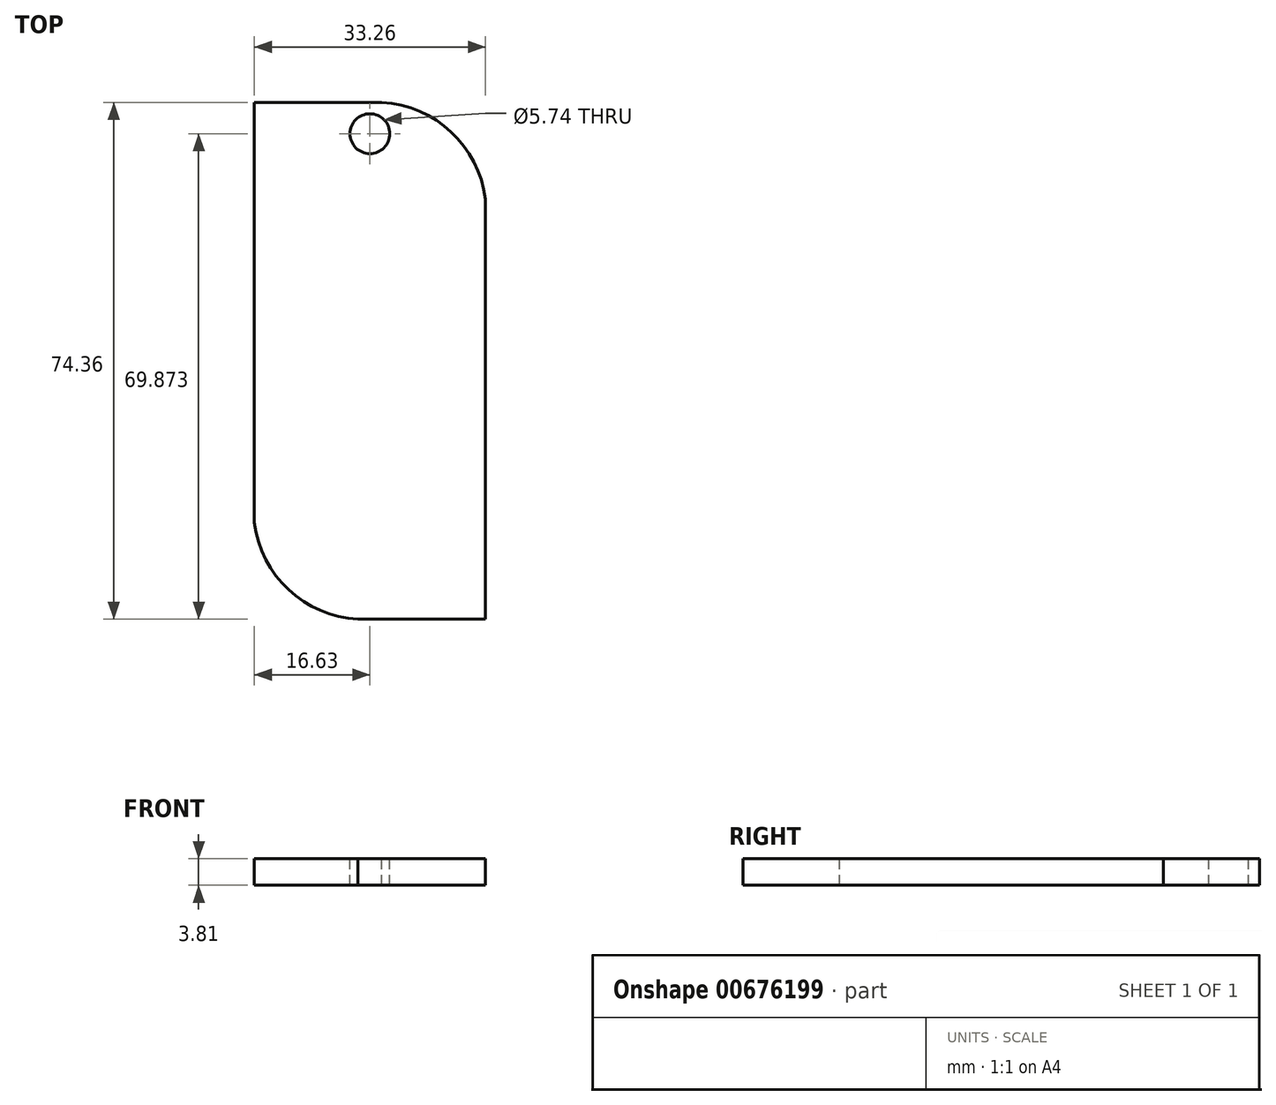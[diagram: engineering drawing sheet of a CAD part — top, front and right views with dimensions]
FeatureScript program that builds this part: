
annotation { "Feature Type Name" : "Feature", "Feature Type Description" : "" }
export const myFeature = defineFeature(function(context is Context, id is Id, definition is map)
    precondition{}
    {
        {
            var Q0;
            Q0=qCreatedBy(makeId("Top.planeOp"),FACE);
            var sketch = newSketch(context, id + "F0", { "sketchPlane" : qUnion([Q0])});
            skLineSegment(sketch, "E0.bottom", {"start": v(-16.63, 37.18) * mm, "end": v(16.63, 37.18) * mm});
            skLineSegment(sketch, "E0.top", {"start": v(-16.63, -37.18) * mm, "end": v(16.63, -37.18) * mm});
            skLineSegment(sketch, "E0.left", {"start": v(-16.63, 37.18) * mm, "end": v(-16.63, -37.18) * mm});
            skLineSegment(sketch, "E0.right", {"start": v(16.63, 37.18) * mm, "end": v(16.63, -37.18) * mm});
            skPoint(sketch, "E0.middle", {"position": v(0, 0) * mm});
            skSolve(sketch);
        }
        {
            var Q0;
            Q0=makeQuery(id+"F0.imprint","IMPRINT",FACE,{"disambiguationData":[TD([[makeQuery(id+"F0.imprint","IMPRINT",EDGE,{"derivedFrom":sQuery(id+"F0.wireOp",EDGE,"E0.bottom")}),-1.0]])]});
            extrude(context, id + "F1", {"entities" : qUnion([Q0]), "depth" : 3.8 * mm, "offsetDistance" : 25.4 * mm});
        }
        {
            var Q0;
            Q0=makeQuery(id+"F1.opExtrude","CAP_FACE",FACE,{"disambiguationData":[OSD([sQuery(id+"F0.wireOp",EDGE,"E0.bottom"),sQuery(id+"F0.wireOp",EDGE,"E0.top"),sQuery(id+"F0.wireOp",EDGE,"E0.left"),sQuery(id+"F0.wireOp",EDGE,"E0.right")])],"isStart":false});
            var sketch = newSketch(context, id + "F2", { "sketchPlane" : qUnion([Q0])});
            skLineSegment(sketch, "E1", {"start": v(0, 37.18) * mm, "end": v(0, -37.18) * mm, "construction": true});
            skArc(sketch, "E2", {"start": v(16.63, 23.28) * mm, "mid": v(11.05, 33.5) * mm, "end": v(0, 37.18) * mm});
            skArc(sketch, "E3.MirrorCS", {"start": v(-16.63, 23.28) * mm, "mid": v(-11.05, 33.5) * mm, "end": v(0, 37.18) * mm});
            skLineSegment(sketch, "E4", {"start": v(-16.63, 0) * mm, "end": v(16.63, 0) * mm, "construction": true});
            skArc(sketch, "E5.MirrorCS", {"start": v(-16.63, -23.28) * mm, "mid": v(-11.05, -33.5) * mm, "end": v(0, -37.18) * mm});
            skArc(sketch, "E6.MirrorCS", {"start": v(16.63, -23.28) * mm, "mid": v(11.05, -33.5) * mm, "end": v(0, -37.18) * mm});
            skCircle(sketch, "E7", {"center": v(0, 32.7) * mm, "radius": 2.87 * mm});
            skSolve(sketch);
        }
        {
            var Q0;
            {var subQ0=sQuery(id+"F2.wireOp",EDGE,"E2");var subQ1=makeQuery(id+"F1.opExtrude","CAP_EDGE",EDGE,{"disambiguationData":[OSD([sQuery(id+"F0.wireOp",EDGE,"E0.right")])],"isStart":false});var subQ2=makeQuery(id+"F2.imprint","INTERSECT",VERTEX,{"derivedFrom":[subQ1,subQ0]});Q0=makeQuery(id+"F2.imprint","IMPRINT",FACE,{"disambiguationData":[TD([[makeQuery(id+"F2.imprint","IMPRINT",EDGE,{"disambiguationData":[TD([[subQ2,-1.0]])],"derivedFrom":subQ0}),-1.0]])]});}
            var Q1;
            {var subQ0=sQuery(id+"F2.wireOp",EDGE,"E3.MirrorCS");var subQ1=makeQuery(id+"F1.opExtrude","CAP_EDGE",EDGE,{"disambiguationData":[OSD([sQuery(id+"F0.wireOp",EDGE,"E0.left")])],"isStart":false});var subQ2=makeQuery(id+"F2.imprint","INTERSECT",VERTEX,{"derivedFrom":[subQ1,subQ0]});Q1=makeQuery(id+"F2.imprint","IMPRINT",FACE,{"disambiguationData":[TD([[makeQuery(id+"F2.imprint","IMPRINT",EDGE,{"disambiguationData":[TD([[subQ2,-1.0]])],"derivedFrom":subQ0}),1.0]])]});}
            var Q2;
            {var subQ0=sQuery(id+"F2.wireOp",EDGE,"E5.MirrorCS");var subQ1=makeQuery(id+"F1.opExtrude","CAP_EDGE",EDGE,{"disambiguationData":[OSD([sQuery(id+"F0.wireOp",EDGE,"E0.left")])],"isStart":false});var subQ2=makeQuery(id+"F2.imprint","INTERSECT",VERTEX,{"derivedFrom":[subQ1,subQ0]});Q2=makeQuery(id+"F2.imprint","IMPRINT",FACE,{"disambiguationData":[TD([[makeQuery(id+"F2.imprint","IMPRINT",EDGE,{"disambiguationData":[TD([[subQ2,-1.0]])],"derivedFrom":subQ0}),-1.0]])]});}
            var Q3;
            {var subQ0=sQuery(id+"F2.wireOp",EDGE,"E6.MirrorCS");var subQ1=makeQuery(id+"F1.opExtrude","CAP_EDGE",EDGE,{"disambiguationData":[OSD([sQuery(id+"F0.wireOp",EDGE,"E0.right")])],"isStart":false});var subQ2=makeQuery(id+"F2.imprint","INTERSECT",VERTEX,{"derivedFrom":[subQ1,subQ0]});Q3=makeQuery(id+"F2.imprint","IMPRINT",FACE,{"disambiguationData":[TD([[makeQuery(id+"F2.imprint","IMPRINT",EDGE,{"disambiguationData":[TD([[subQ2,-1.0]])],"derivedFrom":subQ0}),1.0]])]});}
            var Q4;
            Q4=makeQuery(id+"F2.imprint","IMPRINT",FACE,{"disambiguationData":[TD([[makeQuery(id+"F2.imprint","IMPRINT",EDGE,{"derivedFrom":sQuery(id+"F2.wireOp",EDGE,"E7")}),1.0]])]});
            extrude(context, id + "F3", {"entities" : qUnion([Q0, Q1, Q2, Q3, Q4]), "operationType" : NewBodyOperationType.REMOVE, "endBound" : BoundingType.THROUGH_ALL, "oppositeDirection" : true, "depth" : 25.4 * mm, "offsetDistance" : 25.4 * mm});
        }
    });
